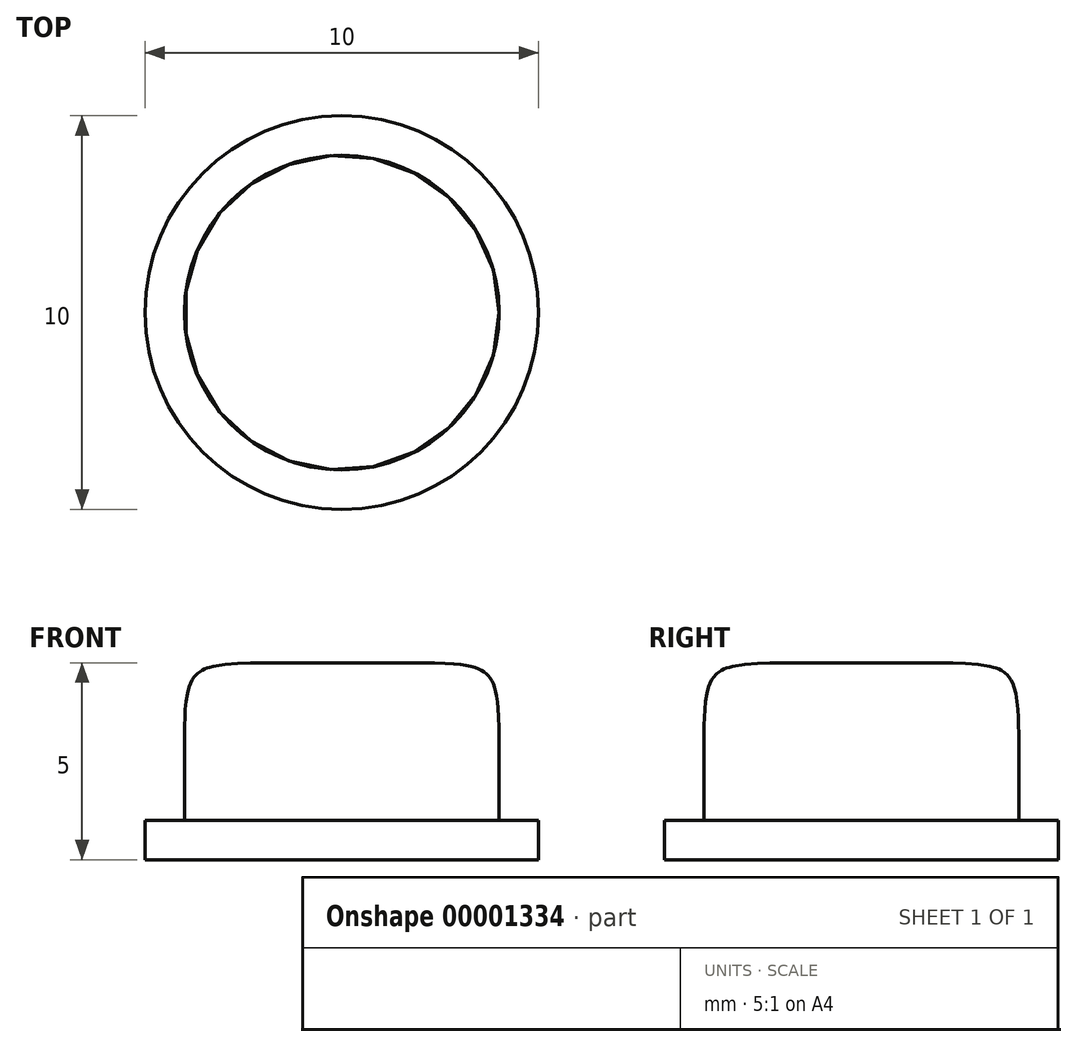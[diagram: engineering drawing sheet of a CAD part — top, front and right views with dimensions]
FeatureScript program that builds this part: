
annotation { "Feature Type Name" : "Feature", "Feature Type Description" : "" }
export const myFeature = defineFeature(function(context is Context, id is Id, definition is map)
    precondition{}
    {
        {
            var Q0;
            Q0=qCreatedBy(makeId("Top.planeOp"),FACE);
            var sketch = newSketch(context, id + "F0", { "sketchPlane" : qUnion([Q0])});
            skCircle(sketch, "E0", {"center": v(0, 0) * mm, "radius": 5 * mm});
            skSolve(sketch);
        }
        {
            var Q0;
            Q0=makeQuery(id+"F0.imprint","IMPRINT",FACE,{"disambiguationData":[TD([[makeQuery(id+"F0.imprint","IMPRINT",EDGE,{"derivedFrom":sQuery(id+"F0.wireOp",EDGE,"E0")}),1.0]])]});
            extrude(context, id + "F1", {"entities" : qUnion([Q0]), "depth" : 1 * mm});
        }
        {
            var Q0;
            Q0=makeQuery(id+"F1.opExtrude","CAP_FACE",FACE,{"disambiguationData":[OSD([sQuery(id+"F0.wireOp",EDGE,"E0")])],"isStart":false});
            var sketch = newSketch(context, id + "F2", { "sketchPlane" : qUnion([Q0])});
            skCircle(sketch, "E1", {"center": v(0, 0) * mm, "radius": 4 * mm});
            skSolve(sketch);
        }
        {
            var Q0;
            Q0=makeQuery(id+"F2.imprint","IMPRINT",FACE,{"disambiguationData":[TD([[makeQuery(id+"F2.imprint","IMPRINT",EDGE,{"derivedFrom":sQuery(id+"F2.wireOp",EDGE,"E1")}),1.0]])]});
            extrude(context, id + "F3", {"entities" : qUnion([Q0]), "operationType" : NewBodyOperationType.ADD, "depth" : 4 * mm});
        }
        {
            var Q0;
            Q0=makeQuery(id+"F3.opExtrude","CAP_FACE",FACE,{"disambiguationData":[OSD([sQuery(id+"F2.wireOp",EDGE,"E1")])],"isStart":false});
            var Q1;
            Q1=makeQuery(id+"F3.opExtrude","CAP_EDGE",EDGE,{"disambiguationData":[OSD([sQuery(id+"F2.wireOp",EDGE,"E1")])],"isStart":false});
            fillet(context, id + "F4", {"entities" : qUnion([Q0, Q1]), "radius" : 2 * mm, "tangentPropagation" : true, "rho" : .7, "crossSection" : FilletCrossSection.CONIC, "allowEdgeOverflow" : false});
        }
    });
